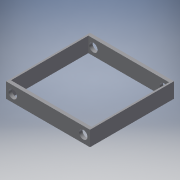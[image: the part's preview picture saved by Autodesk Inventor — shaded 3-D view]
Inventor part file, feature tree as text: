
AUTODESK INVENTOR PART (.ipt)
format: ipt  version: 2018.3 (Build 223284000, 284)  size: 118,784 bytes
history: native  units: mm
features: sketch x4, extrude x3, hole x1
ambient origin geometry x8: Origin, YZ Plane, XZ Plane, XY Plane, X Axis, Y Axis, Z Axis, Center Point
bodies: Solid1 (feature_tree)
feature tree (8):
  extrude  "Extrusion1"  Depth=50.0mm
  extrude  "Extrusion2"  Depth=48.0mm
  extrude  "Extrusion3"  Depth=1.0mm TaperAngle=0.0deg
  hole  "Hole1"  [1 undecoded]
  sketch  "Sketch1"  dims[d0=50.0mm d1=50.0mm]
  sketch  "Sketch2"  dims[d2=48.0mm d3=48.0mm]
  sketch  "Sketch3"  dims[d4=9.0mm d5=0.0mm d6=1.0mm d7=0.0mm]
  sketch  "Sketch4"  dims[d8=1.0mm d9=0.0mm d10=5.0mm d11=6.0mm d12=4.0mm d13=2.0mm d14=90.0deg d15=8.0mm d16=20.594885mm]
note: 1 required parameter value undecoded (feature->parameter linkage not recoverable at this tier; creation-order binding heuristic only, values carry confidence <= 0.55)
